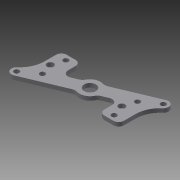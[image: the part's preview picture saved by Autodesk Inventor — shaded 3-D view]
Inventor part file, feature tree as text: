
AUTODESK INVENTOR PART (.ipt)
format: ipt  version: 2015 (Build 190159000, 159)  size: 169,472 bytes
history: native  units: mm
features: reference x7, extrude x1
ambient origin geometry x8: Origin, YZ Plane, XZ Plane, XY Plane, X Axis, Y Axis, Z Axis, Center Point
bodies: Solid1 (feature_tree)
feature tree (8):
  extrude  "Extrusion1"  Depth=4.0mm
  reference  "Reference1"
  reference  "Reference2"
  reference  "Reference3"
  reference  "Reference6"
  reference  "Reference7"
  reference  "Reference8"
  reference  "Reference9"
